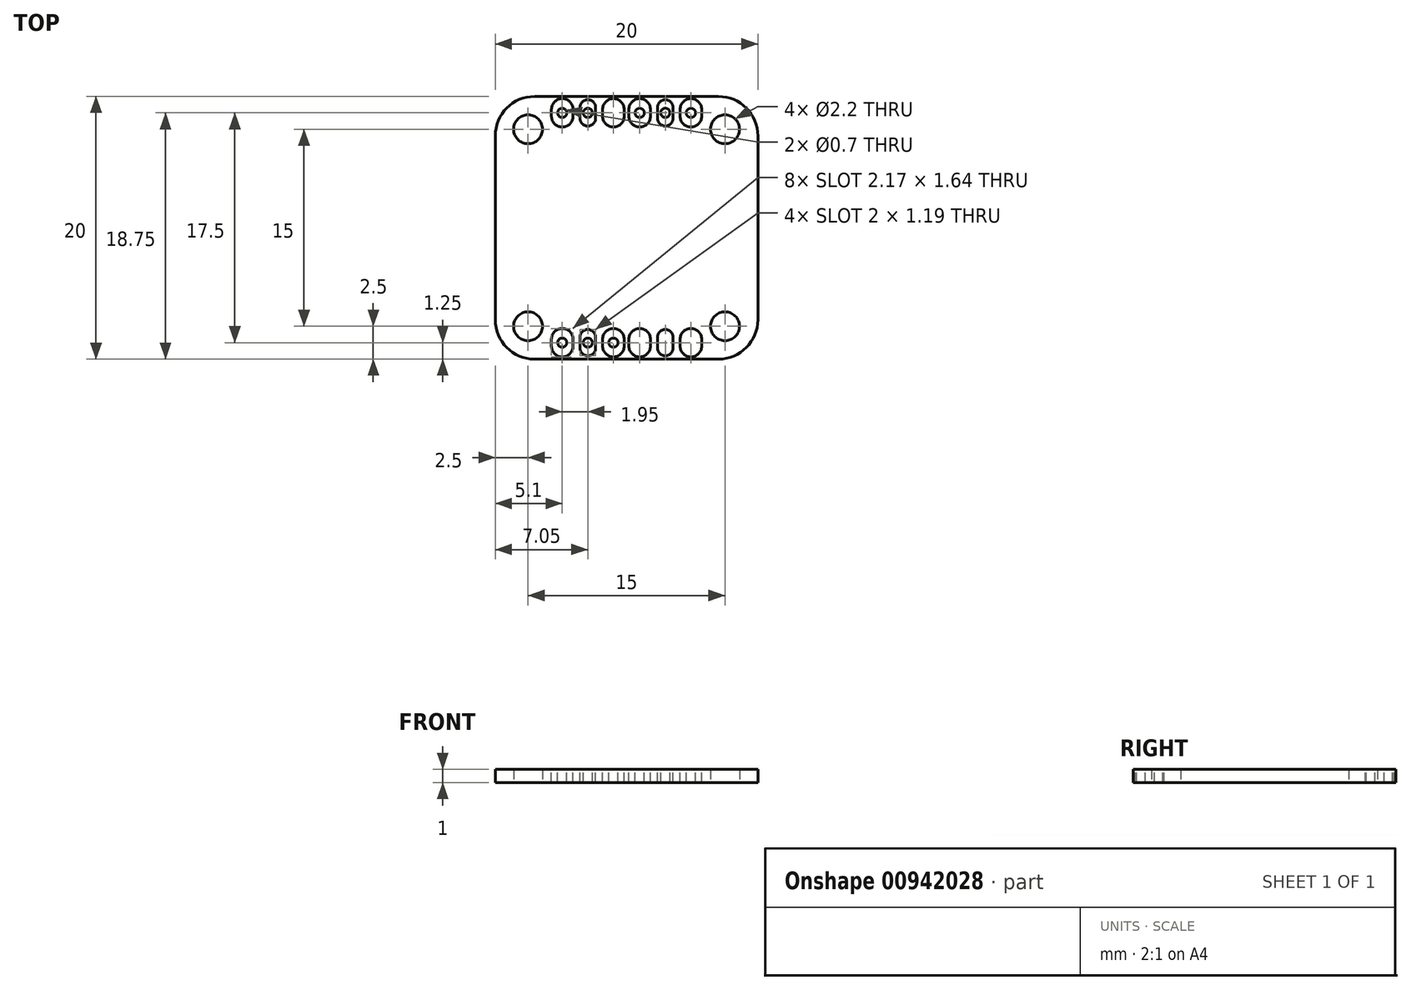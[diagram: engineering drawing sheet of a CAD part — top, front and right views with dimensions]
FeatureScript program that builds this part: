
annotation { "Feature Type Name" : "Feature", "Feature Type Description" : "" }
export const myFeature = defineFeature(function(context is Context, id is Id, definition is map)
    precondition{}
    {
        {
            var Q0;
            Q0=qCreatedBy(makeId("Top.planeOp"),FACE);
            var sketch = newSketch(context, id + "F0", { "sketchPlane" : qUnion([Q0])});
            skLineSegment(sketch, "E0.bottom", {"start": v(10, 10) * mm, "end": v(-10, 10) * mm});
            skLineSegment(sketch, "E0.top", {"start": v(10, -10) * mm, "end": v(-10, -10) * mm});
            skLineSegment(sketch, "E0.left", {"start": v(10, 10) * mm, "end": v(10, -10) * mm});
            skLineSegment(sketch, "E0.right", {"start": v(-10, 10) * mm, "end": v(-10, -10) * mm});
            skPoint(sketch, "E0.middle", {"position": v(0, 0) * mm});
            skCircle(sketch, "E1", {"center": v(-7.5, 7.5) * mm, "radius": 1.1 * mm});
            skCircle(sketch, "E2.1.0", {"center": v(-7.5, -7.5) * mm, "radius": 1.1 * mm});
            skCircle(sketch, "E2.2.0", {"center": v(7.5, -7.5) * mm, "radius": 1.1 * mm});
            skCircle(sketch, "E2.3.0", {"center": v(7.5, 7.5) * mm, "radius": 1.1 * mm});
            skSolve(sketch);
        }
        {
            var Q0;
            Q0=makeQuery(id+"F0.imprint","IMPRINT",FACE,{"disambiguationData":[TD([[makeQuery(id+"F0.imprint","IMPRINT",EDGE,{"derivedFrom":sQuery(id+"F0.wireOp",EDGE,"E0.bottom")}),1.0]])]});
            extrude(context, id + "F1", {"entities" : qUnion([Q0]), "depth" : 1 * mm, "offsetDistance" : 25 * mm});
        }
        {
            var Q0;
            Q0=makeQuery(id+"F1.opExtrude","SWEPT_EDGE",EDGE,{"disambiguationData":[OSD([sQuery(id+"F0.wireOp",EDGE,"E0.top"),sQuery(id+"F0.wireOp",EDGE,"E0.right")])]});
            var Q1;
            Q1=makeQuery(id+"F1.opExtrude","SWEPT_EDGE",EDGE,{"disambiguationData":[OSD([sQuery(id+"F0.wireOp",EDGE,"E0.top"),sQuery(id+"F0.wireOp",EDGE,"E0.left")])]});
            var Q2;
            Q2=makeQuery(id+"F1.opExtrude","SWEPT_EDGE",EDGE,{"disambiguationData":[OSD([sQuery(id+"F0.wireOp",EDGE,"E0.bottom"),sQuery(id+"F0.wireOp",EDGE,"E0.left")])]});
            var Q3;
            Q3=makeQuery(id+"F1.opExtrude","SWEPT_EDGE",EDGE,{"disambiguationData":[OSD([sQuery(id+"F0.wireOp",EDGE,"E0.bottom"),sQuery(id+"F0.wireOp",EDGE,"E0.right")])]});
            fillet(context, id + "F2", {"entities" : qUnion([Q0, Q1, Q2, Q3]), "radius" : 3 * mm, "tangentPropagation" : true, "allowEdgeOverflow" : false});
        }
        {
            var Q0;
            Q0=makeQuery(id+"F1.opExtrude","CAP_FACE",FACE,{"disambiguationData":[OSD([sQuery(id+"F0.wireOp",EDGE,"E0.bottom"),sQuery(id+"F0.wireOp",EDGE,"E0.top"),sQuery(id+"F0.wireOp",EDGE,"E0.left"),sQuery(id+"F0.wireOp",EDGE,"E0.right"),sQuery(id+"F0.wireOp",EDGE,"E1"),sQuery(id+"F0.wireOp",EDGE,"E2.1.0"),sQuery(id+"F0.wireOp",EDGE,"E2.2.0"),sQuery(id+"F0.wireOp",EDGE,"E2.3.0")])],"isStart":false});
            var sketch = newSketch(context, id + "F3", { "sketchPlane" : qUnion([Q0])});
            skCircle(sketch, "E3", {"center": v(-4.9, 8.75) * mm, "radius": 0.35 * mm});
            skLineSegment(sketch, "E4.direction1", {"start": v(-6.18, 8.75) * mm, "end": v(-4.9, 8.75) * mm, "construction": true});
            skArc(sketch, "E5", {"start": v(-5.72, 9.01) * mm, "mid": v(-4.9, 9.83) * mm, "end": v(-4.08, 9.01) * mm});
            skArc(sketch, "E6.MirrorCS", {"start": v(-5.72, 8.49) * mm, "mid": v(-4.9, 7.67) * mm, "end": v(-4.08, 8.49) * mm});
            skLineSegment(sketch, "E7", {"start": v(-5.72, 9.01) * mm, "end": v(-5.72, 8.49) * mm});
            skLineSegment(sketch, "E8", {"start": v(-4.08, 8.49) * mm, "end": v(-4.08, 9.01) * mm});
            skPoint(sketch, "E9", {"position": v(-5.72, 8.75) * mm});
            skCircle(sketch, "E10.1.0.0", {"center": v(-2.95, 8.75) * mm, "radius": 0.35 * mm});
            skCircle(sketch, "E10.2.0.0", {"center": v(-1, 8.75) * mm, "radius": 0.35 * mm});
            skLineSegment(sketch, "E10.direction1", {"start": v(-4.9, 8.75) * mm, "end": v(-2.95, 8.75) * mm, "construction": true});
            skLineSegment(sketch, "E11", {"start": v(-2.95, 9.16) * mm, "end": v(-2.95, 7.97) * mm, "construction": true});
            skLineSegment(sketch, "E12.MirrorCS", {"start": v(-0.18, 9.01) * mm, "end": v(-0.18, 8.49) * mm});
            skLineSegment(sketch, "E13.MirrorCS", {"start": v(-1.82, 8.49) * mm, "end": v(-1.82, 9.01) * mm});
            skArc(sketch, "E14.MirrorCS", {"start": v(-0.18, 8.49) * mm, "mid": v(-1, 7.67) * mm, "end": v(-1.82, 8.49) * mm});
            skArc(sketch, "E15.MirrorCS", {"start": v(-0.18, 9.01) * mm, "mid": v(-1, 9.83) * mm, "end": v(-1.82, 9.01) * mm});
            skArc(sketch, "E16", {"start": v(-3.54, 9.16) * mm, "mid": v(-2.95, 9.75) * mm, "end": v(-2.36, 9.16) * mm});
            skArc(sketch, "E17.MirrorCS", {"start": v(-3.54, 8.34) * mm, "mid": v(-2.95, 7.75) * mm, "end": v(-2.36, 8.34) * mm});
            skLineSegment(sketch, "E18", {"start": v(-3.54, 9.16) * mm, "end": v(-3.54, 8.34) * mm});
            skLineSegment(sketch, "E19", {"start": v(-2.36, 8.34) * mm, "end": v(-2.36, 9.16) * mm});
            skArc(sketch, "E20.MirrorCS", {"start": v(5.72, 9.01) * mm, "mid": v(4.9, 9.83) * mm, "end": v(4.08, 9.01) * mm});
            skLineSegment(sketch, "E21.MirrorCS", {"start": v(4.08, 8.49) * mm, "end": v(4.08, 9.01) * mm});
            skArc(sketch, "E22.MirrorCS", {"start": v(5.72, 8.49) * mm, "mid": v(4.9, 7.67) * mm, "end": v(4.08, 8.49) * mm});
            skLineSegment(sketch, "E23.MirrorCS", {"start": v(5.72, 9.01) * mm, "end": v(5.72, 8.49) * mm});
            skLineSegment(sketch, "E24.MirrorCS", {"start": v(3.54, 9.16) * mm, "end": v(3.54, 8.34) * mm});
            skArc(sketch, "E25.MirrorCS", {"start": v(3.54, 9.16) * mm, "mid": v(2.95, 9.75) * mm, "end": v(2.36, 9.16) * mm});
            skLineSegment(sketch, "E26.MirrorCS", {"start": v(2.36, 8.34) * mm, "end": v(2.36, 9.16) * mm});
            skArc(sketch, "E27.MirrorCS", {"start": v(3.54, 8.34) * mm, "mid": v(2.95, 7.75) * mm, "end": v(2.36, 8.34) * mm});
            skArc(sketch, "E28.MirrorCS", {"start": v(0.18, 8.49) * mm, "mid": v(1, 7.67) * mm, "end": v(1.82, 8.49) * mm});
            skLineSegment(sketch, "E29.MirrorCS", {"start": v(1.82, 8.49) * mm, "end": v(1.82, 9.01) * mm});
            skArc(sketch, "E30.MirrorCS", {"start": v(0.18, 9.01) * mm, "mid": v(1, 9.83) * mm, "end": v(1.82, 9.01) * mm});
            skLineSegment(sketch, "E31.MirrorCS", {"start": v(0.18, 9.01) * mm, "end": v(0.18, 8.49) * mm});
            skCircle(sketch, "E32.MirrorC", {"center": v(1, 8.75) * mm, "radius": 0.35 * mm});
            skCircle(sketch, "E33.MirrorC", {"center": v(2.95, 8.75) * mm, "radius": 0.35 * mm});
            skCircle(sketch, "E34.MirrorC", {"center": v(4.9, 8.75) * mm, "radius": 0.35 * mm});
            skLineSegment(sketch, "E35.MirrorCS", {"start": v(-5.72, -9.01) * mm, "end": v(-5.72, -8.49) * mm});
            skCircle(sketch, "E36.MirrorC", {"center": v(-4.9, -8.75) * mm, "radius": 0.35 * mm});
            skLineSegment(sketch, "E37.MirrorCS", {"start": v(-4.08, -8.49) * mm, "end": v(-4.08, -9.01) * mm});
            skCircle(sketch, "E38.MirrorC", {"center": v(2.95, -8.75) * mm, "radius": 0.35 * mm});
            skLineSegment(sketch, "E39.MirrorCS", {"start": v(1.82, -8.49) * mm, "end": v(1.82, -9.01) * mm});
            skCircle(sketch, "E40.MirrorC", {"center": v(4.9, -8.75) * mm, "radius": 0.35 * mm});
            skLineSegment(sketch, "E41.MirrorCS", {"start": v(-2.36, -8.34) * mm, "end": v(-2.36, -9.16) * mm});
            skArc(sketch, "E42.MirrorCS", {"start": v(5.72, -9.01) * mm, "mid": v(4.9, -9.83) * mm, "end": v(4.08, -9.01) * mm});
            skLineSegment(sketch, "E43.MirrorCS", {"start": v(-3.54, -9.16) * mm, "end": v(-3.54, -8.34) * mm});
            skCircle(sketch, "E44.MirrorC", {"center": v(1, -8.75) * mm, "radius": 0.35 * mm});
            skLineSegment(sketch, "E45.MirrorCS", {"start": v(-6.18, -8.75) * mm, "end": v(-4.9, -8.75) * mm, "construction": true});
            skLineSegment(sketch, "E46.MirrorCS", {"start": v(-4.9, -8.75) * mm, "end": v(-2.95, -8.75) * mm, "construction": true});
            skLineSegment(sketch, "E47.MirrorCS", {"start": v(-2.95, -9.16) * mm, "end": v(-2.95, -7.97) * mm, "construction": true});
            skArc(sketch, "E48.MirrorCS", {"start": v(3.54, -9.16) * mm, "mid": v(2.95, -9.75) * mm, "end": v(2.36, -9.16) * mm});
            skArc(sketch, "E49.MirrorCS", {"start": v(3.54, -8.34) * mm, "mid": v(2.95, -7.75) * mm, "end": v(2.36, -8.34) * mm});
            skLineSegment(sketch, "E50.MirrorCS", {"start": v(5.72, -9.01) * mm, "end": v(5.72, -8.49) * mm});
            skArc(sketch, "E51.MirrorCS", {"start": v(-3.54, -8.34) * mm, "mid": v(-2.95, -7.75) * mm, "end": v(-2.36, -8.34) * mm});
            skLineSegment(sketch, "E52.MirrorCS", {"start": v(3.54, -9.16) * mm, "end": v(3.54, -8.34) * mm});
            skArc(sketch, "E53.MirrorCS", {"start": v(0.18, -8.49) * mm, "mid": v(1, -7.67) * mm, "end": v(1.82, -8.49) * mm});
            skLineSegment(sketch, "E54.MirrorCS", {"start": v(-1.82, -8.49) * mm, "end": v(-1.82, -9.01) * mm});
            skCircle(sketch, "E55.MirrorC", {"center": v(-1, -8.75) * mm, "radius": 0.35 * mm});
            skLineSegment(sketch, "E56.MirrorCS", {"start": v(4.08, -8.49) * mm, "end": v(4.08, -9.01) * mm});
            skPoint(sketch, "E57.MirrorP", {"position": v(-5.72, -8.75) * mm});
            skArc(sketch, "E58.MirrorCS", {"start": v(-5.72, -8.49) * mm, "mid": v(-4.9, -7.67) * mm, "end": v(-4.08, -8.49) * mm});
            skArc(sketch, "E59.MirrorCS", {"start": v(0.18, -9.01) * mm, "mid": v(1, -9.83) * mm, "end": v(1.82, -9.01) * mm});
            skArc(sketch, "E60.MirrorCS", {"start": v(-0.18, -8.49) * mm, "mid": v(-1, -7.67) * mm, "end": v(-1.82, -8.49) * mm});
            skLineSegment(sketch, "E61.MirrorCS", {"start": v(-0.18, -9.01) * mm, "end": v(-0.18, -8.49) * mm});
            skCircle(sketch, "E62.MirrorC", {"center": v(-2.95, -8.75) * mm, "radius": 0.35 * mm});
            skLineSegment(sketch, "E63.MirrorCS", {"start": v(0.18, -9.01) * mm, "end": v(0.18, -8.49) * mm});
            skArc(sketch, "E64.MirrorCS", {"start": v(5.72, -8.49) * mm, "mid": v(4.9, -7.67) * mm, "end": v(4.08, -8.49) * mm});
            skArc(sketch, "E65.MirrorCS", {"start": v(-5.72, -9.01) * mm, "mid": v(-4.9, -9.83) * mm, "end": v(-4.08, -9.01) * mm});
            skArc(sketch, "E66.MirrorCS", {"start": v(-0.18, -9.01) * mm, "mid": v(-1, -9.83) * mm, "end": v(-1.82, -9.01) * mm});
            skLineSegment(sketch, "E67.MirrorCS", {"start": v(2.36, -8.34) * mm, "end": v(2.36, -9.16) * mm});
            skArc(sketch, "E68.MirrorCS", {"start": v(-3.54, -9.16) * mm, "mid": v(-2.95, -9.75) * mm, "end": v(-2.36, -9.16) * mm});
            skSolve(sketch);
        }
        {
            var Q0;
            Q0=makeQuery(id+"F3.imprint","IMPRINT",FACE,{"disambiguationData":[TD([[makeQuery(id+"F3.imprint","IMPRINT",EDGE,{"derivedFrom":sQuery(id+"F3.wireOp",EDGE,"E3")}),-1.0]])]});
            var Q1;
            Q1=makeQuery(id+"F3.imprint","IMPRINT",FACE,{"disambiguationData":[TD([[makeQuery(id+"F3.imprint","IMPRINT",EDGE,{"derivedFrom":sQuery(id+"F3.wireOp",EDGE,"E3")}),1.0]])]});
            var Q2;
            Q2=makeQuery(id+"F3.imprint","IMPRINT",FACE,{"disambiguationData":[TD([[makeQuery(id+"F3.imprint","IMPRINT",EDGE,{"derivedFrom":sQuery(id+"F3.wireOp",EDGE,"E10.1.0.0")}),-1.0]])]});
            var Q3;
            Q3=makeQuery(id+"F3.imprint","IMPRINT",FACE,{"disambiguationData":[TD([[makeQuery(id+"F3.imprint","IMPRINT",EDGE,{"derivedFrom":sQuery(id+"F3.wireOp",EDGE,"E10.1.0.0")}),1.0]])]});
            var Q4;
            Q4=makeQuery(id+"F3.imprint","IMPRINT",FACE,{"disambiguationData":[TD([[makeQuery(id+"F3.imprint","IMPRINT",EDGE,{"derivedFrom":sQuery(id+"F3.wireOp",EDGE,"E10.2.0.0")}),-1.0]])]});
            var Q5;
            Q5=makeQuery(id+"F3.imprint","IMPRINT",FACE,{"disambiguationData":[TD([[makeQuery(id+"F3.imprint","IMPRINT",EDGE,{"derivedFrom":sQuery(id+"F3.wireOp",EDGE,"E10.2.0.0")}),1.0]])]});
            var Q6;
            Q6=makeQuery(id+"F3.imprint","IMPRINT",FACE,{"disambiguationData":[TD([[makeQuery(id+"F3.imprint","IMPRINT",EDGE,{"derivedFrom":sQuery(id+"F3.wireOp",EDGE,"E28.MirrorCS")}),1.0]])]});
            var Q7;
            Q7=makeQuery(id+"F3.imprint","IMPRINT",FACE,{"disambiguationData":[TD([[makeQuery(id+"F3.imprint","IMPRINT",EDGE,{"derivedFrom":sQuery(id+"F3.wireOp",EDGE,"E32.MirrorC")}),-1.0]])]});
            var Q8;
            Q8=makeQuery(id+"F3.imprint","IMPRINT",FACE,{"disambiguationData":[TD([[makeQuery(id+"F3.imprint","IMPRINT",EDGE,{"derivedFrom":sQuery(id+"F3.wireOp",EDGE,"E33.MirrorC")}),-1.0]])]});
            var Q9;
            Q9=makeQuery(id+"F3.imprint","IMPRINT",FACE,{"disambiguationData":[TD([[makeQuery(id+"F3.imprint","IMPRINT",EDGE,{"derivedFrom":sQuery(id+"F3.wireOp",EDGE,"E34.MirrorC")}),-1.0]])]});
            var Q10;
            Q10=makeQuery(id+"F3.imprint","IMPRINT",FACE,{"disambiguationData":[TD([[makeQuery(id+"F3.imprint","IMPRINT",EDGE,{"derivedFrom":sQuery(id+"F3.wireOp",EDGE,"E20.MirrorCS")}),1.0]])]});
            var Q11;
            Q11=makeQuery(id+"F3.imprint","IMPRINT",FACE,{"disambiguationData":[TD([[makeQuery(id+"F3.imprint","IMPRINT",EDGE,{"derivedFrom":sQuery(id+"F3.wireOp",EDGE,"E24.MirrorCS")}),-1.0]])]});
            var Q12;
            Q12=makeQuery(id+"F3.imprint","IMPRINT",FACE,{"disambiguationData":[TD([[makeQuery(id+"F3.imprint","IMPRINT",EDGE,{"derivedFrom":sQuery(id+"F3.wireOp",EDGE,"E40.MirrorC")}),-1.0]])]});
            var Q13;
            Q13=makeQuery(id+"F3.imprint","IMPRINT",FACE,{"disambiguationData":[TD([[makeQuery(id+"F3.imprint","IMPRINT",EDGE,{"derivedFrom":sQuery(id+"F3.wireOp",EDGE,"E40.MirrorC")}),1.0]])]});
            var Q14;
            Q14=makeQuery(id+"F3.imprint","IMPRINT",FACE,{"disambiguationData":[TD([[makeQuery(id+"F3.imprint","IMPRINT",EDGE,{"derivedFrom":sQuery(id+"F3.wireOp",EDGE,"E38.MirrorC")}),-1.0]])]});
            var Q15;
            Q15=makeQuery(id+"F3.imprint","IMPRINT",FACE,{"disambiguationData":[TD([[makeQuery(id+"F3.imprint","IMPRINT",EDGE,{"derivedFrom":sQuery(id+"F3.wireOp",EDGE,"E38.MirrorC")}),1.0]])]});
            var Q16;
            Q16=makeQuery(id+"F3.imprint","IMPRINT",FACE,{"disambiguationData":[TD([[makeQuery(id+"F3.imprint","IMPRINT",EDGE,{"derivedFrom":sQuery(id+"F3.wireOp",EDGE,"E39.MirrorCS")}),-1.0]])]});
            var Q17;
            Q17=makeQuery(id+"F3.imprint","IMPRINT",FACE,{"disambiguationData":[TD([[makeQuery(id+"F3.imprint","IMPRINT",EDGE,{"derivedFrom":sQuery(id+"F3.wireOp",EDGE,"E44.MirrorC")}),1.0]])]});
            var Q18;
            Q18=makeQuery(id+"F3.imprint","IMPRINT",FACE,{"disambiguationData":[TD([[makeQuery(id+"F3.imprint","IMPRINT",EDGE,{"derivedFrom":sQuery(id+"F3.wireOp",EDGE,"E54.MirrorCS")}),1.0]])]});
            var Q19;
            Q19=makeQuery(id+"F3.imprint","IMPRINT",FACE,{"disambiguationData":[TD([[makeQuery(id+"F3.imprint","IMPRINT",EDGE,{"derivedFrom":sQuery(id+"F3.wireOp",EDGE,"E55.MirrorC")}),-1.0]])]});
            var Q20;
            Q20=makeQuery(id+"F3.imprint","IMPRINT",FACE,{"disambiguationData":[TD([[makeQuery(id+"F3.imprint","IMPRINT",EDGE,{"derivedFrom":sQuery(id+"F3.wireOp",EDGE,"E62.MirrorC")}),-1.0]])]});
            var Q21;
            Q21=makeQuery(id+"F3.imprint","IMPRINT",FACE,{"disambiguationData":[TD([[makeQuery(id+"F3.imprint","IMPRINT",EDGE,{"derivedFrom":sQuery(id+"F3.wireOp",EDGE,"E41.MirrorCS")}),-1.0]])]});
            var Q22;
            Q22=makeQuery(id+"F3.imprint","IMPRINT",FACE,{"disambiguationData":[TD([[makeQuery(id+"F3.imprint","IMPRINT",EDGE,{"derivedFrom":sQuery(id+"F3.wireOp",EDGE,"E36.MirrorC")}),-1.0]])]});
            var Q23;
            Q23=makeQuery(id+"F3.imprint","IMPRINT",FACE,{"disambiguationData":[TD([[makeQuery(id+"F3.imprint","IMPRINT",EDGE,{"derivedFrom":sQuery(id+"F3.wireOp",EDGE,"E35.MirrorCS")}),-1.0]])]});
            extrude(context, id + "F4", {"entities" : qUnion([Q0, Q1, Q2, Q3, Q4, Q5, Q6, Q7, Q8, Q9, Q10, Q11, Q12, Q13, Q14, Q15, Q16, Q17, Q18, Q19, Q20, Q21, Q22, Q23]), "operationType" : NewBodyOperationType.REMOVE, "oppositeDirection" : true, "depth" : 25 * mm, "offsetDistance" : 25 * mm});
        }
        {
            var Q0;
            Q0=makeQuery(id+"F3.imprint","IMPRINT",FACE,{"disambiguationData":[TD([[makeQuery(id+"F3.imprint","IMPRINT",EDGE,{"derivedFrom":sQuery(id+"F3.wireOp",EDGE,"E3")}),-1.0]])]});
            var Q1;
            Q1=makeQuery(id+"F3.imprint","IMPRINT",FACE,{"disambiguationData":[TD([[makeQuery(id+"F3.imprint","IMPRINT",EDGE,{"derivedFrom":sQuery(id+"F3.wireOp",EDGE,"E10.1.0.0")}),-1.0]])]});
            extrude(context, id + "F5", {"entities" : qUnion([Q0, Q1]), "oppositeDirection" : true, "depth" : 1 * mm, "offsetDistance" : 25 * mm});
        }
    });
